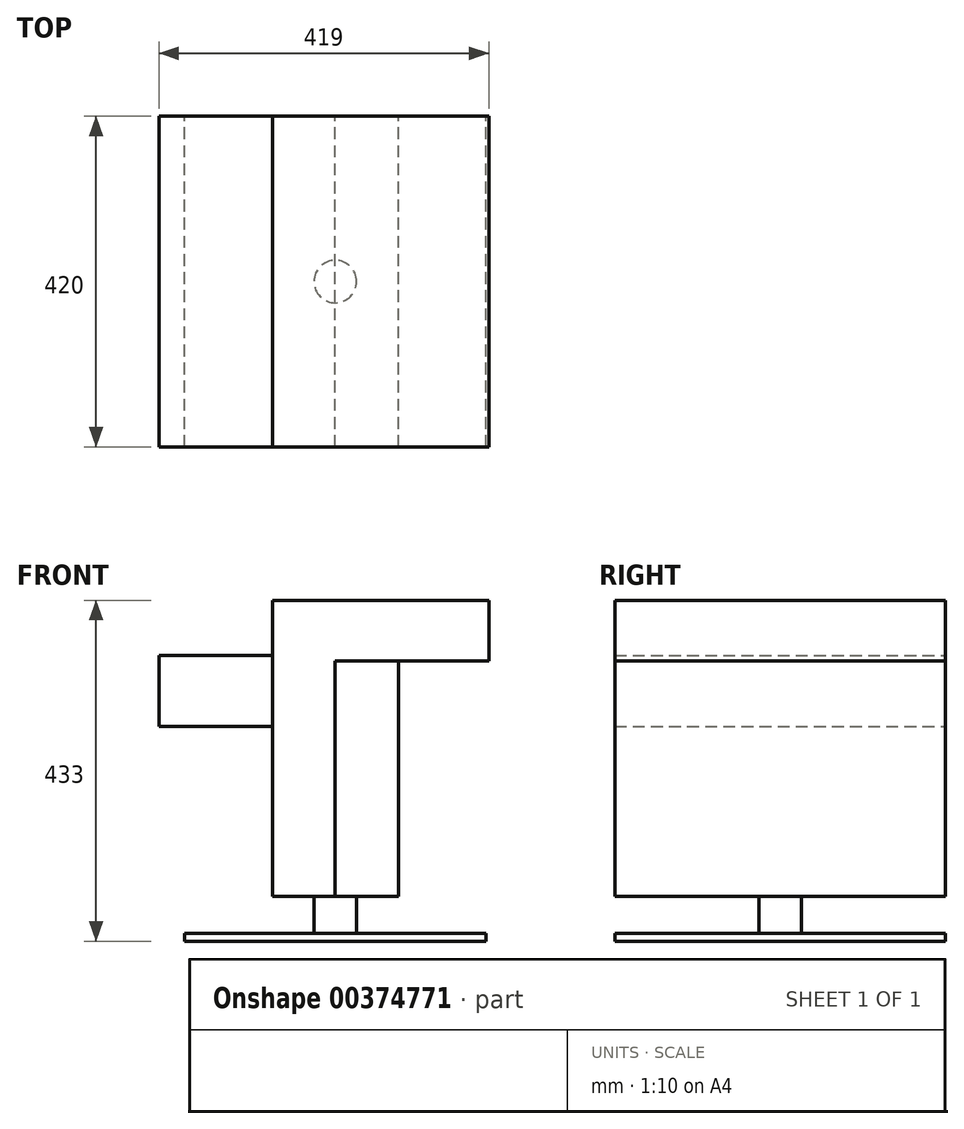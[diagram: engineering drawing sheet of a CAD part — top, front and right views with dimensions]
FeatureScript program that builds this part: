
annotation { "Feature Type Name" : "Feature", "Feature Type Description" : "" }
export const myFeature = defineFeature(function(context is Context, id is Id, definition is map)
    precondition{}
    {
        {
            var Q0;
            Q0=qCreatedBy(makeId("Front.planeOp"),FACE);
            var sketch = newSketch(context, id + "F0", { "sketchPlane" : qUnion([Q0])});
            skLineSegment(sketch, "E0.bottom", {"start": v(-80, 188) * mm, "end": v(195, 188) * mm});
            skLineSegment(sketch, "E0.top", {"start": v(0, 111) * mm, "end": v(195, 111) * mm});
            skLineSegment(sketch, "E0.right", {"start": v(195, 188) * mm, "end": v(195, 111) * mm});
            skLineSegment(sketch, "E1.top", {"start": v(-80, -188) * mm, "end": v(0, -188) * mm});
            skLineSegment(sketch, "E1.left", {"start": v(-80, 188) * mm, "end": v(-80, -188) * mm});
            skLineSegment(sketch, "E1.right", {"start": v(0, 111) * mm, "end": v(0, -188) * mm});
            skSolve(sketch);
        }
        {
            var Q0;
            Q0=qCreatedBy(makeId("Front.planeOp"),FACE);
            var sketch = newSketch(context, id + "F1", { "sketchPlane" : qUnion([Q0])});
            skLineSegment(sketch, "E2.right", {"start": v(0, 111) * mm, "end": v(0, -188) * mm});
            skLineSegment(sketch, "E3.bottom", {"start": v(0, -188) * mm, "end": v(80, -188) * mm});
            skLineSegment(sketch, "E3.top", {"start": v(0, 111) * mm, "end": v(80, 111) * mm});
            skLineSegment(sketch, "E3.left", {"start": v(0, -188) * mm, "end": v(0, 111) * mm});
            skLineSegment(sketch, "E3.right", {"start": v(80, -188) * mm, "end": v(80, 111) * mm});
            skLineSegment(sketch, "E4.bottom", {"start": v(-80, 118) * mm, "end": v(-224, 118) * mm});
            skLineSegment(sketch, "E4.top", {"start": v(-80, 28) * mm, "end": v(-224, 28) * mm});
            skLineSegment(sketch, "E4.left", {"start": v(-80, 118) * mm, "end": v(-80, 28) * mm});
            skLineSegment(sketch, "E4.right", {"start": v(-224, 118) * mm, "end": v(-224, 28) * mm});
            skLineSegment(sketch, "E5", {"start": v(0, 111) * mm, "end": v(-80, 111) * mm, "construction": true});
            skSolve(sketch);
        }
        {
            var Q0;
            Q0 = qSketchRegion(id + "F0", true);
            extrude(context, id + "F2", {"entities" : qUnion([Q0]), "depth" : 420 / 2 * mm, "hasSecondDirection" : true, "secondDirectionOppositeDirection" : true, "secondDirectionDepth" : 420 / 2 * mm});
        }
        {
            var Q0;
            Q0 = qSketchRegion(id + "F1", true);
            extrude(context, id + "F3", {"entities" : qUnion([Q0]), "depth" : 420 / 2 * mm, "hasSecondDirection" : true, "secondDirectionOppositeDirection" : true, "secondDirectionDepth" : 420 / 2 * mm});
        }
        {
            var Q0;
            Q0=qCreatedBy(makeId("Front.planeOp"),FACE);
            var sketch = newSketch(context, id + "F4", { "sketchPlane" : qUnion([Q0])});
            skLineSegment(sketch, "E6.bottom", {"start": v(-27, -235) * mm, "end": v(0, -235) * mm});
            skLineSegment(sketch, "E6.top", {"start": v(-27, -188) * mm, "end": v(0, -188) * mm});
            skLineSegment(sketch, "E6.left", {"start": v(-27, -235) * mm, "end": v(-27, -188) * mm});
            skLineSegment(sketch, "E6.right", {"start": v(0, -235) * mm, "end": v(0, -188) * mm});
            skSolve(sketch);
        }
        {
            var Q0;
            Q0=qCreatedBy(makeId("Front.planeOp"),FACE);
            var sketch = newSketch(context, id + "F5", { "sketchPlane" : qUnion([Q0])});
            skLineSegment(sketch, "E7.bottom", {"start": v(-191.5, -235) * mm, "end": v(191.5, -235) * mm});
            skLineSegment(sketch, "E7.top", {"start": v(-191.5, -245) * mm, "end": v(191.5, -245) * mm});
            skLineSegment(sketch, "E7.left", {"start": v(-191.5, -235) * mm, "end": v(-191.5, -245) * mm});
            skLineSegment(sketch, "E7.right", {"start": v(191.5, -235) * mm, "end": v(191.5, -245) * mm});
            skSolve(sketch);
        }
        {
            var Q0;
            Q0=makeQuery(id+"F4.imprint","IMPRINT",FACE,{"disambiguationData":[TD([[makeQuery(id+"F4.imprint","IMPRINT",EDGE,{"derivedFrom":sQuery(id+"F4.wireOp",EDGE,"E6.bottom")}),1.0]])]});
            var Q1;
            Q1=sQuery(id+"F4.wireOp",EDGE,"E6.right");
            revolve(context, id + "F6", {"entities" : qUnion([Q0]), "axis" : qUnion([Q1]), "revolveType" : RevolveType.FULL});
        }
        {
            var Q0;
            Q0 = qSketchRegion(id + "F5", true);
            extrude(context, id + "F7", {"entities" : qUnion([Q0]), "operationType" : NewBodyOperationType.ADD, "depth" : 210 * mm, "hasSecondDirection" : true, "secondDirectionOppositeDirection" : true, "secondDirectionDepth" : 210 * mm});
        }
    });
